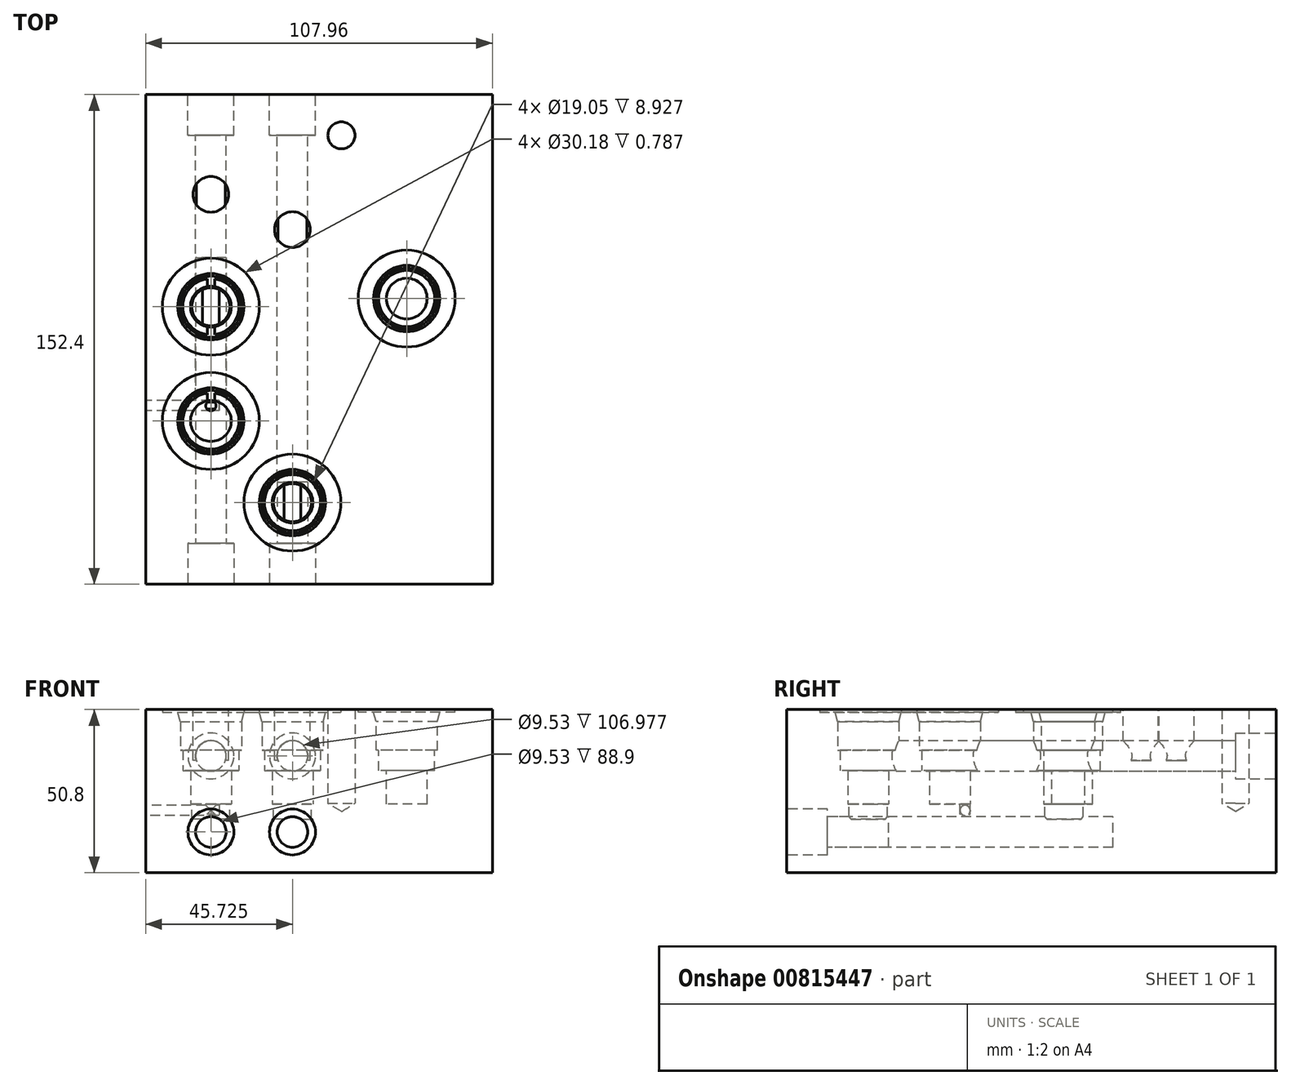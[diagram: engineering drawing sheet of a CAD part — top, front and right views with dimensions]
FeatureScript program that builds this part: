
annotation { "Feature Type Name" : "Feature", "Feature Type Description" : "" }
export const myFeature = defineFeature(function(context is Context, id is Id, definition is map)
    precondition{}
    {
        {
            var Q0;
            Q0=qCreatedBy(makeId("Top.planeOp"),FACE);
            var sketch = newSketch(context, id + "F0", { "sketchPlane" : qUnion([Q0])});
            skLineSegment(sketch, "E0.bottom", {"start": v(53.98, -76.2) * mm, "end": v(-53.97, -76.2) * mm});
            skLineSegment(sketch, "E0.top", {"start": v(53.98, 76.2) * mm, "end": v(-53.97, 76.2) * mm});
            skLineSegment(sketch, "E0.left", {"start": v(53.98, -76.2) * mm, "end": v(53.98, 76.2) * mm});
            skLineSegment(sketch, "E0.right", {"start": v(-53.97, -76.2) * mm, "end": v(-53.97, 76.2) * mm});
            skPoint(sketch, "E0.middle", {"position": v(0, 0) * mm});
            skSolve(sketch);
        }
        {
            var Q0;
            Q0 = qSketchRegion(id + "F0", true);
            extrude(context, id + "F1", {"entities" : qUnion([Q0]), "endBound" : BoundingType.SYMMETRIC, "depth" : 50.8 * mm, "offsetDistance" : 25.4 * mm});
        }
        {
            var Q0;
            Q0=qCreatedBy(makeId("Front.planeOp"),FACE);
            cPlane(context, id + "F2", {"entities" : qUnion([Q0]), "cplaneType" : CPlaneType.OFFSET, "offset" : 50.8 * mm, "width" : 152.4 * mm, "height" : 152.4 * mm});
        }
        {
            var Q0;
            Q0=qCreatedBy(id+"F2.planeOp",FACE);
            var sketch = newSketch(context, id + "F3", { "sketchPlane" : qUnion([Q0])});
            skLineSegment(sketch, "E1", {"start": v(-8.25, 23.88) * mm, "end": v(-8.25, -15.65) * mm, "construction": true});
            skLineSegment(sketch, "E2", {"start": v(-8.25, 25.4) * mm, "end": v(6.83, 25.4) * mm});
            skLineSegment(sketch, "E3", {"start": v(6.83, 25.4) * mm, "end": v(6.83, 24.61) * mm});
            skLineSegment(sketch, "E4", {"start": v(6.83, 24.61) * mm, "end": v(2.07, 24.61) * mm});
            skLineSegment(sketch, "E5", {"start": v(2.07, 24.61) * mm, "end": v(1.27, 21.63) * mm});
            skLineSegment(sketch, "E6", {"start": v(1.27, 21.63) * mm, "end": v(1.27, 12.7) * mm});
            skLineSegment(sketch, "E7", {"start": v(1.27, 12.7) * mm, "end": v(0.48, 12.7) * mm});
            skLineSegment(sketch, "E8", {"start": v(0.48, 12.7) * mm, "end": v(0.48, 6.35) * mm});
            skLineSegment(sketch, "E9", {"start": v(0.48, 6.35) * mm, "end": v(-1.9, 6.35) * mm});
            skLineSegment(sketch, "E10", {"start": v(-1.9, 6.35) * mm, "end": v(-1.9, -3.96) * mm});
            skLineSegment(sketch, "E11", {"start": v(-1.9, -3.96) * mm, "end": v(-8.25, -3.96) * mm});
            skLineSegment(sketch, "E12", {"start": v(-8.25, -3.96) * mm, "end": v(-8.25, 25.4) * mm});
            skSolve(sketch);
        }
        {
            var Q0;
            Q0 = qSketchRegion(id + "F3", true);
            var Q1;
            Q1=sQuery(id+"F3.wireOp",EDGE,"E1");
            revolve(context, id + "F4", {"operationType" : NewBodyOperationType.REMOVE, "surfaceOperationType" : NewSurfaceOperationType.NEW, "entities" : qUnion([Q0]), "axis" : qUnion([Q1]), "revolveType" : RevolveType.FULL, "oppositeDirection" : true});
        }
        {
            var Q0;
            Q0=qCreatedBy(makeId("Front.planeOp"),FACE);
            cPlane(context, id + "F5", {"entities" : qUnion([Q0]), "cplaneType" : CPlaneType.OFFSET, "offset" : 25.4 * mm, "width" : 152.4 * mm, "height" : 152.4 * mm});
        }
        {
            var Q0;
            Q0=qCreatedBy(id+"F5.planeOp",FACE);
            var sketch = newSketch(context, id + "F6", { "sketchPlane" : qUnion([Q0])});
            skLineSegment(sketch, "E13", {"start": v(-33.65, 30.59) * mm, "end": v(-33.65, -15.65) * mm, "construction": true});
            skLineSegment(sketch, "E14", {"start": v(-33.65, 25.4) * mm, "end": v(-18.57, 25.4) * mm});
            skLineSegment(sketch, "E15", {"start": v(-18.57, 25.4) * mm, "end": v(-18.57, 24.61) * mm});
            skLineSegment(sketch, "E16", {"start": v(-18.57, 24.61) * mm, "end": v(-23.33, 24.61) * mm});
            skLineSegment(sketch, "E17", {"start": v(-23.33, 24.61) * mm, "end": v(-24.13, 21.63) * mm});
            skLineSegment(sketch, "E18", {"start": v(-24.13, 21.63) * mm, "end": v(-24.13, 12.7) * mm});
            skLineSegment(sketch, "E19", {"start": v(-24.13, 12.7) * mm, "end": v(-24.92, 12.7) * mm});
            skLineSegment(sketch, "E20", {"start": v(-24.92, 12.7) * mm, "end": v(-24.92, 6.35) * mm});
            skLineSegment(sketch, "E21", {"start": v(-24.92, 6.35) * mm, "end": v(-27.3, 6.35) * mm});
            skLineSegment(sketch, "E22", {"start": v(-27.3, 6.35) * mm, "end": v(-27.3, -3.96) * mm});
            skLineSegment(sketch, "E23", {"start": v(-27.3, -3.96) * mm, "end": v(-33.65, -3.96) * mm});
            skLineSegment(sketch, "E24", {"start": v(-33.65, -3.96) * mm, "end": v(-33.65, 25.4) * mm});
            skSolve(sketch);
        }
        {
            var Q0;
            Q0 = qSketchRegion(id + "F6", true);
            var Q1;
            Q1=sQuery(id+"F6.wireOp",EDGE,"E13");
            revolve(context, id + "F7", {"operationType" : NewBodyOperationType.REMOVE, "surfaceOperationType" : NewSurfaceOperationType.NEW, "entities" : qUnion([Q0]), "axis" : qUnion([Q1]), "revolveType" : RevolveType.FULL, "oppositeDirection" : true});
        }
        {
            var Q0;
            Q0=qCreatedBy(makeId("Front.planeOp"),FACE);
            cPlane(context, id + "F8", {"entities" : qUnion([Q0]), "cplaneType" : CPlaneType.OFFSET, "offset" : 63.5 * mm, "oppositeDirection" : true, "width" : 152.4 * mm, "height" : 152.4 * mm});
        }
        {
            var Q0;
            Q0=qCreatedBy(id+"F8.planeOp",FACE);
            var sketch = newSketch(context, id + "F9", { "sketchPlane" : qUnion([Q0])});
            skLineSegment(sketch, "E25", {"start": v(6.99, 29.82) * mm, "end": v(6.99, -15.65) * mm, "construction": true});
            skLineSegment(sketch, "E26", {"start": v(11.2, 25.4) * mm, "end": v(11.2, -3.82) * mm});
            skLineSegment(sketch, "E27", {"start": v(11.2, -3.82) * mm, "end": v(6.99, -6.35) * mm});
            skLineSegment(sketch, "E28", {"start": v(11.2, 25.4) * mm, "end": v(6.99, 25.4) * mm});
            skLineSegment(sketch, "E29", {"start": v(6.99, 25.4) * mm, "end": v(6.99, -6.35) * mm});
            skSolve(sketch);
        }
        {
            var Q0;
            Q0 = qSketchRegion(id + "F9", true);
            var Q1;
            Q1=sQuery(id+"F9.wireOp",EDGE,"E25");
            revolve(context, id + "F10", {"operationType" : NewBodyOperationType.REMOVE, "surfaceOperationType" : NewSurfaceOperationType.NEW, "entities" : qUnion([Q0]), "axis" : qUnion([Q1]), "revolveType" : RevolveType.FULL, "oppositeDirection" : true});
        }
        {
            var Q0;
            Q0=qCreatedBy(makeId("Front.planeOp"),FACE);
            cPlane(context, id + "F11", {"entities" : qUnion([Q0]), "cplaneType" : CPlaneType.OFFSET, "offset" : 12.7 * mm, "oppositeDirection" : true, "width" : 152.4 * mm, "height" : 152.4 * mm});
        }
        {
            var Q0;
            Q0=qCreatedBy(id+"F11.planeOp",FACE);
            var sketch = newSketch(context, id + "F12", { "sketchPlane" : qUnion([Q0])});
            skLineSegment(sketch, "E30", {"start": v(27.3, 28.6) * mm, "end": v(27.3, -10.93) * mm, "construction": true});
            skLineSegment(sketch, "E31", {"start": v(27.3, 25.4) * mm, "end": v(42.4, 25.4) * mm});
            skLineSegment(sketch, "E32", {"start": v(42.4, 25.4) * mm, "end": v(42.4, 24.61) * mm});
            skLineSegment(sketch, "E33", {"start": v(42.4, 24.61) * mm, "end": v(37.63, 24.61) * mm});
            skLineSegment(sketch, "E34", {"start": v(37.63, 24.61) * mm, "end": v(36.83, 21.63) * mm});
            skLineSegment(sketch, "E35", {"start": v(36.83, 21.63) * mm, "end": v(36.83, 12.7) * mm});
            skLineSegment(sketch, "E36", {"start": v(36.83, 12.7) * mm, "end": v(36.04, 12.7) * mm});
            skLineSegment(sketch, "E37", {"start": v(36.04, 12.7) * mm, "end": v(36.04, 6.35) * mm});
            skLineSegment(sketch, "E38", {"start": v(36.04, 6.35) * mm, "end": v(33.66, 6.35) * mm});
            skLineSegment(sketch, "E39", {"start": v(33.66, 6.35) * mm, "end": v(33.66, -3.96) * mm});
            skLineSegment(sketch, "E40", {"start": v(33.66, -3.96) * mm, "end": v(27.3, -3.96) * mm});
            skLineSegment(sketch, "E41", {"start": v(27.3, -3.96) * mm, "end": v(27.3, 25.4) * mm});
            skSolve(sketch);
        }
        {
            var Q0;
            Q0 = qSketchRegion(id + "F12", true);
            var Q1;
            Q1=sQuery(id+"F12.wireOp",EDGE,"E30");
            revolve(context, id + "F13", {"operationType" : NewBodyOperationType.REMOVE, "surfaceOperationType" : NewSurfaceOperationType.NEW, "entities" : qUnion([Q0]), "axis" : qUnion([Q1]), "revolveType" : RevolveType.FULL});
        }
        {
            var Q0;
            Q0=qCreatedBy(makeId("Front.planeOp"),FACE);
            cPlane(context, id + "F14", {"entities" : qUnion([Q0]), "cplaneType" : CPlaneType.OFFSET, "offset" : 10.16 * mm, "oppositeDirection" : true, "width" : 152.4 * mm, "height" : 152.4 * mm});
        }
        {
            var Q0;
            Q0=qCreatedBy(id+"F14.planeOp",FACE);
            var sketch = newSketch(context, id + "F15", { "sketchPlane" : qUnion([Q0])});
            skLineSegment(sketch, "E42", {"start": v(-33.65, 30.01) * mm, "end": v(-33.65, -9.52) * mm, "construction": true});
            skLineSegment(sketch, "E43", {"start": v(-33.65, 25.4) * mm, "end": v(-18.57, 25.4) * mm});
            skLineSegment(sketch, "E44", {"start": v(-18.57, 25.4) * mm, "end": v(-18.57, 24.61) * mm});
            skLineSegment(sketch, "E45", {"start": v(-18.57, 24.61) * mm, "end": v(-23.33, 24.61) * mm});
            skLineSegment(sketch, "E46", {"start": v(-23.33, 24.61) * mm, "end": v(-24.13, 21.63) * mm});
            skLineSegment(sketch, "E47", {"start": v(-24.13, 21.63) * mm, "end": v(-24.13, 12.7) * mm});
            skLineSegment(sketch, "E48", {"start": v(-24.13, 12.7) * mm, "end": v(-24.92, 12.7) * mm});
            skLineSegment(sketch, "E49", {"start": v(-24.92, 12.7) * mm, "end": v(-24.92, 6.35) * mm});
            skLineSegment(sketch, "E50", {"start": v(-24.92, 6.35) * mm, "end": v(-27.3, 6.35) * mm});
            skLineSegment(sketch, "E51", {"start": v(-27.3, 6.35) * mm, "end": v(-27.3, -3.96) * mm});
            skLineSegment(sketch, "E52", {"start": v(-27.3, -3.96) * mm, "end": v(-33.65, -3.96) * mm});
            skLineSegment(sketch, "E53", {"start": v(-33.65, -3.96) * mm, "end": v(-33.65, 25.4) * mm});
            skSolve(sketch);
        }
        {
            var Q0;
            Q0 = qSketchRegion(id + "F15", true);
            var Q1;
            Q1=sQuery(id+"F15.wireOp",EDGE,"E42");
            revolve(context, id + "F16", {"operationType" : NewBodyOperationType.REMOVE, "surfaceOperationType" : NewSurfaceOperationType.NEW, "entities" : qUnion([Q0]), "axis" : qUnion([Q1]), "revolveType" : RevolveType.FULL, "oppositeDirection" : true});
        }
        {
            var Q0;
            Q0=makeQuery(id+"F1.opExtrude","CAP_FACE",FACE,{"disambiguationData":[OSD([sQuery(id+"F0.wireOp",EDGE,"E0.bottom"),sQuery(id+"F0.wireOp",EDGE,"E0.top"),sQuery(id+"F0.wireOp",EDGE,"E0.left"),sQuery(id+"F0.wireOp",EDGE,"E0.right")])],"isStart":false});
            var sketch = newSketch(context, id + "F17", { "sketchPlane" : qUnion([Q0])});
            skCircle(sketch, "E54", {"center": v(-33.65, 10.16) * mm, "radius": 25.4 * mm});
            skCircle(sketch, "E55", {"center": v(-33.65, -25.4) * mm, "radius": 25.4 * mm});
            skCircle(sketch, "E56", {"center": v(27.3, 12.7) * mm, "radius": 25.4 * mm});
            skCircle(sketch, "E57", {"center": v(-8.25, -50.8) * mm, "radius": 25.4 * mm});
            skSolve(sketch);
        }
        {
            var Q0;
            Q0=makeQuery(id+"F1.opExtrude","SWEPT_FACE",FACE,{"disambiguationData":[OSD([sQuery(id+"F0.wireOp",EDGE,"E0.bottom")])]});
            var sketch = newSketch(context, id + "F18", { "sketchPlane" : qUnion([Q0])});
            skCircle(sketch, "E58", {"center": v(-33.66, -12.7) * mm, "radius": 7.14 * mm});
            skSolve(sketch);
        }
        {
            var Q0;
            Q0 = qSketchRegion(id + "F18", true);
            var Q1;
            Q1=sQuery(id+"F17.wireOp",VERTEX,"E54.center");
            extrude(context, id + "F19", {"entities" : qUnion([Q0]), "operationType" : NewBodyOperationType.REMOVE, "oppositeDirection" : true, "depth" : 12.7 * mm, "endBoundEntityVertex" : qUnion([Q1]), "offsetDistance" : 25.4 * mm});
        }
        {
            var Q0;
            Q0=makeQuery(id+"F1.opExtrude","SWEPT_FACE",FACE,{"disambiguationData":[OSD([sQuery(id+"F0.wireOp",EDGE,"E0.bottom")])]});
            var sketch = newSketch(context, id + "F20", { "sketchPlane" : qUnion([Q0])});
            skCircle(sketch, "E59", {"center": v(-33.66, -12.7) * mm, "radius": 4.76 * mm});
            skSolve(sketch);
        }
        {
            var Q0;
            Q0 = qSketchRegion(id + "F20", true);
            extrude(context, id + "F21", {"entities" : qUnion([Q0]), "operationType" : NewBodyOperationType.REMOVE, "oppositeDirection" : true, "depth" : 101.6 * mm, "offsetDistance" : 25.4 * mm});
        }
        {
            var Q0;
            Q0=makeQuery(id+"F1.opExtrude","SWEPT_FACE",FACE,{"disambiguationData":[OSD([sQuery(id+"F0.wireOp",EDGE,"E0.top")])]});
            var sketch = newSketch(context, id + "F22", { "sketchPlane" : qUnion([Q0])});
            skCircle(sketch, "E60", {"center": v(33.65, 10.97) * mm, "radius": 7.14 * mm});
            skSolve(sketch);
        }
        {
            var Q0;
            Q0 = qSketchRegion(id + "F22", true);
            extrude(context, id + "F23", {"entities" : qUnion([Q0]), "operationType" : NewBodyOperationType.REMOVE, "oppositeDirection" : true, "depth" : 12.7 * mm, "offsetDistance" : 25.4 * mm});
        }
        {
            var Q0;
            Q0=makeQuery(id+"F1.opExtrude","SWEPT_FACE",FACE,{"disambiguationData":[OSD([sQuery(id+"F0.wireOp",EDGE,"E0.top")])]});
            var sketch = newSketch(context, id + "F24", { "sketchPlane" : qUnion([Q0])});
            skCircle(sketch, "E61", {"center": v(33.65, 10.97) * mm, "radius": 4.76 * mm});
            skSolve(sketch);
        }
        {
            var Q0;
            Q0 = qSketchRegion(id + "F24", true);
            extrude(context, id + "F25", {"entities" : qUnion([Q0]), "operationType" : NewBodyOperationType.REMOVE, "oppositeDirection" : true, "depth" : 101.6 * mm, "offsetDistance" : 25.4 * mm});
        }
        {
            var Q0;
            Q0=makeQuery(id+"F16.boolean.opBoolean","COPY",FACE,{"derivedFrom":makeQuery(id+"F16.opRevolve","SWEPT_FACE",FACE,{"disambiguationData":[OSD([sQuery(id+"F15.wireOp",EDGE,"E52")])]})});
            var sketch = newSketch(context, id + "F26", { "sketchPlane" : qUnion([Q0])});
            skCircle(sketch, "E62", {"center": v(-33.65, 10.16) * mm, "radius": 5.94 * mm});
            skSolve(sketch);
        }
        {
            var Q0;
            Q0 = qSketchRegion(id + "F26", true);
            extrude(context, id + "F27", {"entities" : qUnion([Q0]), "operationType" : NewBodyOperationType.REMOVE, "oppositeDirection" : true, "depth" : 4.78 * mm, "offsetDistance" : 25.4 * mm});
        }
        {
            var Q0;
            Q0=makeQuery(id+"F7.boolean.opBoolean","COPY",FACE,{"derivedFrom":makeQuery(id+"F7.opRevolve","SWEPT_FACE",FACE,{"disambiguationData":[OSD([sQuery(id+"F6.wireOp",EDGE,"E23")])]})});
            var sketch = newSketch(context, id + "F28", { "sketchPlane" : qUnion([Q0])});
            skLineSegment(sketch, "E63", {"start": v(-27.3, -25.4) * mm, "end": v(-40, -25.4) * mm, "construction": true});
            skLineSegment(sketch, "E64", {"start": v(-33.65, -19.05) * mm, "end": v(-33.65, -31.75) * mm, "construction": true});
            skCircle(sketch, "E65", {"center": v(-33.65, -20.64) * mm, "radius": 1.59 * mm});
            skSolve(sketch);
        }
        {
            var Q0;
            Q0 = qSketchRegion(id + "F28", true);
            extrude(context, id + "F29", {"entities" : qUnion([Q0]), "operationType" : NewBodyOperationType.REMOVE, "oppositeDirection" : true, "depth" : 3.17 * mm, "offsetDistance" : 25.4 * mm});
        }
        {
            var Q0;
            Q0=makeQuery(id+"F1.opExtrude","SWEPT_FACE",FACE,{"disambiguationData":[OSD([sQuery(id+"F0.wireOp",EDGE,"E0.right")])]});
            var sketch = newSketch(context, id + "F30", { "sketchPlane" : qUnion([Q0])});
            skCircle(sketch, "E66", {"center": v(20.64, -5.97) * mm, "radius": 1.59 * mm});
            skLineSegment(sketch, "E67", {"start": v(20.64, -3.96) * mm, "end": v(20.64, -7.14) * mm, "construction": true});
            skLineSegment(sketch, "E68.0.0", {"start": v(19.05, -7.14) * mm, "end": v(22.22, -7.14) * mm});
            skLineSegment(sketch, "E69.0", {"start": v(19.05, -3.96) * mm, "end": v(22.22, -3.96) * mm});
            skSolve(sketch);
        }
        {
            var Q0;
            Q0 = qSketchRegion(id + "F30", true);
            extrude(context, id + "F31", {"entities" : qUnion([Q0]), "operationType" : NewBodyOperationType.REMOVE, "oppositeDirection" : true, "depth" : 22.86 * mm, "offsetDistance" : 25.4 * mm});
        }
        {
            var Q0;
            Q0=makeQuery(id+"F1.opExtrude","SWEPT_FACE",FACE,{"disambiguationData":[OSD([sQuery(id+"F0.wireOp",EDGE,"E0.top")])]});
            var sketch = newSketch(context, id + "F32", { "sketchPlane" : qUnion([Q0])});
            skCircle(sketch, "E70", {"center": v(8.25, 10.97) * mm, "radius": 4.76 * mm});
            skCircle(sketch, "E71", {"center": v(8.25, 10.97) * mm, "radius": 7.14 * mm});
            skLineSegment(sketch, "E72", {"start": v(8.25, 10.97) * mm, "end": v(33.65, 10.97) * mm, "construction": true});
            skLineSegment(sketch, "E73.0.0", {"start": v(1.9, -3.96) * mm, "end": v(14.6, -3.96) * mm});
            skLineSegment(sketch, "E74", {"start": v(8.25, 10.97) * mm, "end": v(8.25, -3.96) * mm, "construction": true});
            skSolve(sketch);
        }
        {
            var Q0;
            Q0=makeQuery(id+"F32.imprint","IMPRINT",FACE,{"disambiguationData":[TD([[makeQuery(id+"F32.imprint","IMPRINT",EDGE,{"derivedFrom":sQuery(id+"F32.wireOp",EDGE,"E70")}),-1.0]])]});
            var Q1;
            Q1=makeQuery(id+"F32.imprint","IMPRINT",FACE,{"disambiguationData":[TD([[makeQuery(id+"F32.imprint","IMPRINT",EDGE,{"derivedFrom":sQuery(id+"F32.wireOp",EDGE,"E70")}),1.0]])]});
            var Q2;
            Q2=makeQuery(id+"F23.boolean.opBoolean","COPY",FACE,{"derivedFrom":makeQuery(id+"F23.opExtrude","CAP_FACE",FACE,{"disambiguationData":[OSD([sQuery(id+"F22.wireOp",EDGE,"E60")])],"isStart":false})});
            extrude(context, id + "F33", {"entities" : qUnion([Q0, Q1]), "operationType" : NewBodyOperationType.REMOVE, "endBound" : BoundingType.UP_TO_SURFACE, "oppositeDirection" : true, "depth" : 25.4 * mm, "endBoundEntityFace" : qUnion([Q2]), "offsetDistance" : 25.4 * mm});
        }
        {
            var Q0;
            Q0=makeQuery(id+"F32.imprint","IMPRINT",FACE,{"disambiguationData":[TD([[makeQuery(id+"F32.imprint","IMPRINT",EDGE,{"derivedFrom":sQuery(id+"F32.wireOp",EDGE,"E70")}),1.0]])]});
            var Q1;
            Q1=makeQuery(id+"F4.boolean.opBoolean","COPY",FACE,{"derivedFrom":makeQuery(id+"F4.opRevolve","SWEPT_FACE",FACE,{"disambiguationData":[OSD([sQuery(id+"F3.wireOp",EDGE,"E8")])]})});
            extrude(context, id + "F34", {"entities" : qUnion([Q0]), "operationType" : NewBodyOperationType.REMOVE, "endBound" : BoundingType.UP_TO_SURFACE, "oppositeDirection" : true, "depth" : 25.4 * mm, "endBoundEntityFace" : qUnion([Q1]), "offsetDistance" : 25.4 * mm});
        }
        {
            var Q0;
            Q0=makeQuery(id+"F1.opExtrude","SWEPT_FACE",FACE,{"disambiguationData":[OSD([sQuery(id+"F0.wireOp",EDGE,"E0.bottom")])]});
            var sketch = newSketch(context, id + "F35", { "sketchPlane" : qUnion([Q0])});
            skCircle(sketch, "E75", {"center": v(-8.25, -12.7) * mm, "radius": 4.76 * mm});
            skCircle(sketch, "E76", {"center": v(-8.25, -12.7) * mm, "radius": 7.14 * mm});
            skLineSegment(sketch, "E77.0.0", {"start": v(-14.6, -3.96) * mm, "end": v(-1.9, -3.96) * mm});
            skLineSegment(sketch, "E78", {"start": v(-8.25, -12.7) * mm, "end": v(-8.25, -3.96) * mm, "construction": true});
            skLineSegment(sketch, "E79", {"start": v(-8.25, -12.7) * mm, "end": v(-33.66, -12.7) * mm, "construction": true});
            skSolve(sketch);
        }
        {
            var Q0;
            {var subQ0=sQuery(id+"F35.wireOp",EDGE,"E75");Q0=makeQuery(id+"F35.imprint","IMPRINT",FACE,{"disambiguationData":[TD([[makeQuery(id+"F35.imprint","IMPRINT",EDGE,{"derivedFrom":subQ0}),-1.0]])]});}
            var Q1;
            {var subQ0=sQuery(id+"F35.wireOp",EDGE,"E77.0.0");var subQ1=sQuery(id+"F35.wireOp",EDGE,"E76");var subQ2=makeQuery(id+"F35.imprint","INTERSECT",VERTEX,{"disambiguationData":[OD(0.0)],"derivedFrom":[subQ1,subQ0]});Q1=makeQuery(id+"F35.imprint","IMPRINT",FACE,{"disambiguationData":[TD([[makeQuery(id+"F35.imprint","IMPRINT",EDGE,{"disambiguationData":[TD([[subQ2,1.0]])],"derivedFrom":subQ1}),1.0]])]});}
            var Q2;
            Q2=makeQuery(id+"F19.boolean.opBoolean","COPY",FACE,{"derivedFrom":makeQuery(id+"F19.opExtrude","CAP_FACE",FACE,{"disambiguationData":[OSD([sQuery(id+"F18.wireOp",EDGE,"E58")])],"isStart":false})});
            extrude(context, id + "F36", {"entities" : qUnion([Q0, Q1]), "operationType" : NewBodyOperationType.REMOVE, "endBound" : BoundingType.UP_TO_SURFACE, "oppositeDirection" : true, "depth" : 25.4 * mm, "endBoundEntityFace" : qUnion([Q2]), "offsetDistance" : 25.4 * mm});
        }
        {
            var Q0;
            Q0=makeQuery(id+"F4.boolean.opBoolean","COPY",FACE,{"derivedFrom":makeQuery(id+"F4.opRevolve","SWEPT_FACE",FACE,{"disambiguationData":[OSD([sQuery(id+"F3.wireOp",EDGE,"E11")])]})});
            var sketch = newSketch(context, id + "F37", { "sketchPlane" : qUnion([Q0])});
            skCircle(sketch, "E80", {"center": v(-8.25, -50.8) * mm, "radius": 5.94 * mm});
            skSolve(sketch);
        }
        {
            var Q0;
            Q0=makeQuery(id+"F37.imprint","IMPRINT",FACE,{"disambiguationData":[TD([[makeQuery(id+"F37.imprint","IMPRINT",EDGE,{"derivedFrom":sQuery(id+"F37.wireOp",EDGE,"E80")}),1.0]])]});
            var Q1;
            Q1=makeQuery(id+"F27.boolean.opBoolean","COPY",FACE,{"disambiguationData":[OD(1.0)],"derivedFrom":makeQuery(id+"F27.opExtrude","CAP_FACE",FACE,{"disambiguationData":[OSD([sQuery(id+"F26.wireOp",EDGE,"E62")])],"isStart":false})});
            extrude(context, id + "F38", {"entities" : qUnion([Q0]), "operationType" : NewBodyOperationType.REMOVE, "endBound" : BoundingType.UP_TO_SURFACE, "oppositeDirection" : true, "depth" : 25.4 * mm, "endBoundEntityFace" : qUnion([Q1]), "offsetDistance" : 25.4 * mm});
        }
        {
            var Q0;
            Q0=makeQuery(id+"F36.boolean.opBoolean","SPLIT",FACE,{"disambiguationData":[TD([makeQuery(id+"F36.opExtrude","SWEPT_FACE",FACE,{"disambiguationData":[OSD([sQuery(id+"F35.wireOp",EDGE,"E75")])]})])],"derivedFrom":makeQuery(id+"F1.opExtrude","SWEPT_FACE",FACE,{"disambiguationData":[OSD([sQuery(id+"F0.wireOp",EDGE,"E0.bottom")])]})});
            extrude(context, id + "F39", {"entities" : qUnion([Q0]), "operationType" : NewBodyOperationType.REMOVE, "oppositeDirection" : true, "depth" : 31.75 * mm, "offsetDistance" : 25.4 * mm});
        }
        {
            var Q0;
            Q0=makeQuery(id+"F1.opExtrude","CAP_FACE",FACE,{"disambiguationData":[OSD([sQuery(id+"F0.wireOp",EDGE,"E0.bottom"),sQuery(id+"F0.wireOp",EDGE,"E0.top"),sQuery(id+"F0.wireOp",EDGE,"E0.left"),sQuery(id+"F0.wireOp",EDGE,"E0.right")])],"isStart":false});
            var sketch = newSketch(context, id + "F40", { "sketchPlane" : qUnion([Q0])});
            skCircle(sketch, "E81", {"center": v(-8.25, 34.18) * mm, "radius": 5.56 * mm});
            skCircle(sketch, "E82", {"center": v(-33.65, 45.13) * mm, "radius": 5.56 * mm});
            skLineSegment(sketch, "E83", {"start": v(-28.9, 63.5) * mm, "end": v(-28.9, 17.49) * mm, "construction": true});
            skLineSegment(sketch, "E84", {"start": v(-38.42, 17.49) * mm, "end": v(-38.42, 63.5) * mm, "construction": true});
            skLineSegment(sketch, "E85", {"start": v(-3.5, 63.5) * mm, "end": v(-3.5, -43.47) * mm, "construction": true});
            skLineSegment(sketch, "E86", {"start": v(-13.02, -43.47) * mm, "end": v(-13.02, 63.5) * mm, "construction": true});
            skLineSegment(sketch, "E87", {"start": v(-3.5, 34.18) * mm, "end": v(-13.02, 34.18) * mm, "construction": true});
            skLineSegment(sketch, "E88", {"start": v(-28.9, 45.13) * mm, "end": v(-38.42, 45.13) * mm, "construction": true});
            skSolve(sketch);
        }
        {
            var Q0;
            Q0=makeQuery(id+"F40.imprint","IMPRINT",FACE,{"disambiguationData":[TD([[makeQuery(id+"F40.imprint","IMPRINT",EDGE,{"derivedFrom":sQuery(id+"F40.wireOp",EDGE,"E81")}),1.0]])]});
            var Q1;
            Q1=makeQuery(id+"F40.imprint","IMPRINT",FACE,{"disambiguationData":[TD([[makeQuery(id+"F40.imprint","IMPRINT",EDGE,{"derivedFrom":sQuery(id+"F40.wireOp",EDGE,"E82")}),1.0]])]});
            extrude(context, id + "F41", {"entities" : qUnion([Q0, Q1]), "operationType" : NewBodyOperationType.REMOVE, "oppositeDirection" : true, "depth" : 15.88 * mm, "offsetDistance" : 25.4 * mm});
        }
    });
